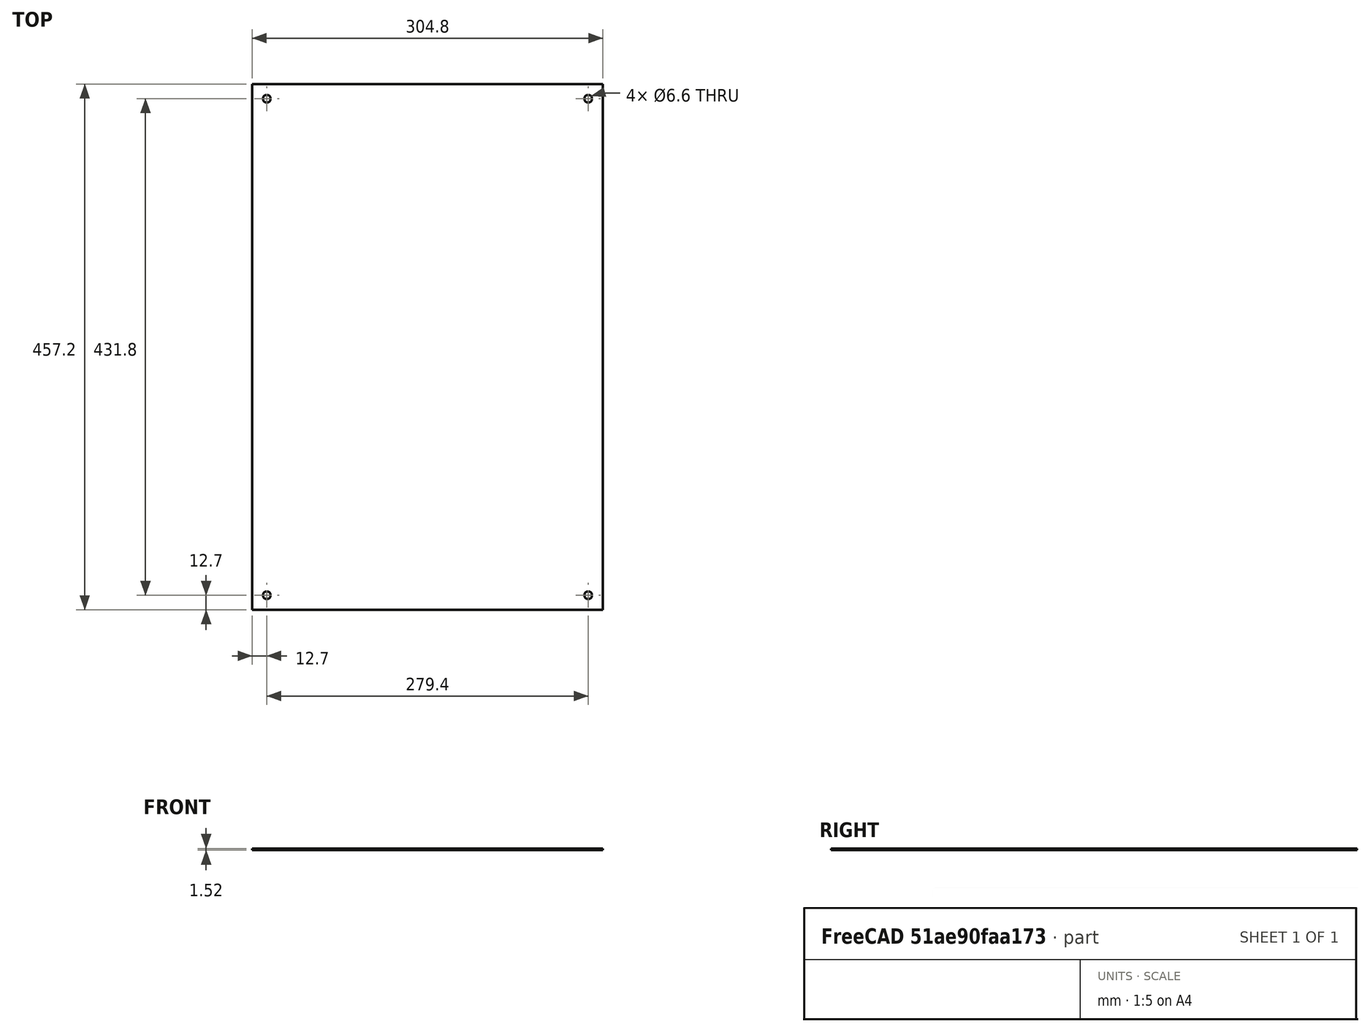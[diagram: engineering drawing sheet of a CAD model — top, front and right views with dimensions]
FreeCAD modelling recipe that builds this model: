
FCSTD DOCUMENT  (FreeCAD 0.21R33694 (Git))
Label: Steel_Sheet_12inx18inx16ga
License: All rights reserved
LicenseURL: http://en.wikipedia.org/wiki/All_rights_reserved
objects: Sketcher::SketchObject×1, PartDesign::Pad×1, PartDesign::Body×1
note: 4 computed .brp shape members not serialized (recipe doc carries the construction recipe); baked Part::Feature solids carry a one-line shape summary decoded from their .brp

FEATURE [Sketcher::SketchObject] Sketch
  FullyConstrained = true
  MapMode = 5
  Support = -> [XY_Plane]
  sketch-geometry (16):
    g0: LineSegment StartX=-152.4 StartY=228.6 StartZ=0 EndX=152.4 EndY=228.6 EndZ=0
    g1: LineSegment StartX=152.4 StartY=228.6 StartZ=0 EndX=152.4 EndY=-228.6 EndZ=0
    g2: LineSegment StartX=152.4 StartY=-228.6 StartZ=0 EndX=-152.4 EndY=-228.6 EndZ=0
    g3: LineSegment StartX=-152.4 StartY=-228.6 StartZ=0 EndX=-152.4 EndY=228.6 EndZ=0
    g4: LineSegment StartX=152.4 StartY=228.6 StartZ=0 EndX=139.7 EndY=228.6 EndZ=0
    g5: LineSegment StartX=139.7 StartY=228.6 StartZ=0 EndX=139.7 EndY=215.9 EndZ=0
    g6: Circle CenterX=139.7 CenterY=215.9 CenterZ=0 NormalX=0 NormalY=0 NormalZ=1 AngleXU=0 Radius=3.3
    g7: LineSegment StartX=-152.4 StartY=228.6 StartZ=0 EndX=-139.7 EndY=228.6 EndZ=0
    g8: LineSegment StartX=-139.7 StartY=228.6 StartZ=0 EndX=-139.7 EndY=215.9 EndZ=0
    g9: Circle CenterX=-139.7 CenterY=215.9 CenterZ=0 NormalX=0 NormalY=0 NormalZ=1 AngleXU=0 Radius=3.3
    g10: LineSegment StartX=-152.4 StartY=-228.6 StartZ=0 EndX=-139.7 EndY=-228.6 EndZ=0
    g11: LineSegment StartX=-139.7 StartY=-228.6 StartZ=0 EndX=-139.7 EndY=-215.9 EndZ=0
    g12: Circle CenterX=-139.7 CenterY=-215.9 CenterZ=0 NormalX=0 NormalY=0 NormalZ=1 AngleXU=0 Radius=3.3
    g13: LineSegment StartX=152.4 StartY=-228.6 StartZ=0 EndX=139.7 EndY=-228.6 EndZ=0
    g14: LineSegment StartX=139.7 StartY=-228.6 StartZ=0 EndX=139.7 EndY=-215.9 EndZ=0
    g15: Circle CenterX=139.7 CenterY=-215.9 CenterZ=0 NormalX=0 NormalY=0 NormalZ=1 AngleXU=0 Radius=3.3
  constraints (43):
    c: Coincident(g0,g1)
    c: Coincident(g1,g2)
    c: Coincident(g2,g3)
    c: Coincident(g3,g0)
    c: Horizontal(g0)
    c: Horizontal(g2)
    c: Vertical(g1)
    c: Vertical(g3)
    c: Symmetric(g2,g0,g-1)
    c: DistanceX(g0,g0) = 304.8
    c: Coincident(g4,g5)
    c: Horizontal(g4)
    c: Vertical(g5)
    c: Coincident(g4,g0)
    c: DistanceX(g4,g4) = 12.7
    c: Coincident(g6,g5)
    c: Coincident(g7,g8)
    c: Horizontal(g7)
    c: Vertical(g8)
    c: Coincident(g7,g0)
    c: Coincident(g9,g8)
    c: Coincident(g10,g11)
    c: Horizontal(g10)
    c: Vertical(g11)
    c: Coincident(g10,g2)
    c: Coincident(g12,g11)
    c: Coincident(g13,g14)
    c: Horizontal(g13)
    c: Vertical(g14)
    c: Coincident(g13,g1)
    c: Coincident(g15,g14)
    c: DistanceY(g1,g1) = 457.2
    c: Horizontal(g9,g6)
    c: Horizontal(g12,g15)
    c: Vertical(g6,g15)
    c: Vertical(g12,g9)
    c: DistanceX(g7,g7) = 12.7
    c: DistanceY(g8,g8) = 12.7
    c: Diameter(g9) = 6.6
    c: Equal(g6,g9)
    c: Equal(g9,g12)
    c: Equal(g12,g15)
    c: DistanceY(g11,g11) = 12.7
FEATURE [PartDesign::Pad] Pad
  Direction = (0,0,1)
  Length = 1.519
  Length2 = 10
  Profile = -> Sketch
  ReferenceAxis = -> Sketch [N_Axis]
  Type = 0
FEATURE [PartDesign::Body] Body
  Group = -> [Sketch,Pad]
  Origin = -> Origin
  Tip = -> Pad
